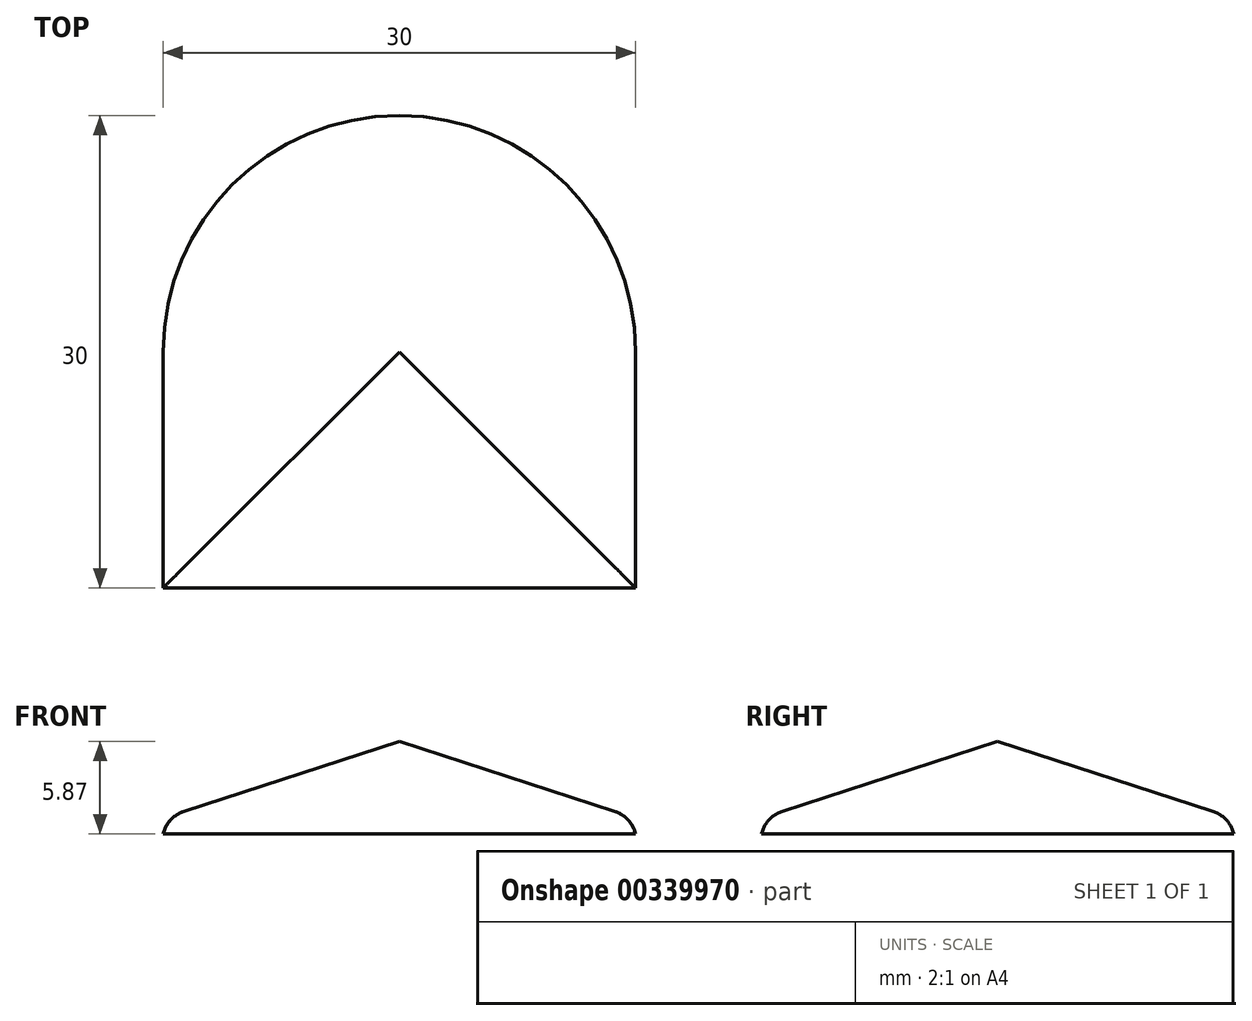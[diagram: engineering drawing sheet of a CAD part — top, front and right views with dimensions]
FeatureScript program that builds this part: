
annotation { "Feature Type Name" : "Feature", "Feature Type Description" : "" }
export const myFeature = defineFeature(function(context is Context, id is Id, definition is map)
    precondition{}
    {
        {
            var Q0;
            Q0=qCreatedBy(makeId("Top.planeOp"),FACE);
            var sketch = newSketch(context, id + "F0", { "sketchPlane" : qUnion([Q0])});
            skLineSegment(sketch, "E0.bottom", {"start": v(0, 15) * mm, "end": v(0, 15) * mm});
            skLineSegment(sketch, "E0.top", {"start": v(-15, -15) * mm, "end": v(15, -15) * mm});
            skLineSegment(sketch, "E0.left", {"start": v(-15, 0) * mm, "end": v(-15, -15) * mm});
            skLineSegment(sketch, "E0.right", {"start": v(15, 0) * mm, "end": v(15, -15) * mm});
            skPoint(sketch, "E0.middle", {"position": v(0, 0) * mm});
            skPoint(sketch, "E1.visualSharp", {"position": v(-15, 15) * mm});
            skArc(sketch, "E1.filletArc", {"start": v(0, 15) * mm, "mid": v(-10.6, 10.6) * mm, "end": v(-15, 0) * mm});
            skPoint(sketch, "E2.visualSharp", {"position": v(15, 15) * mm});
            skArc(sketch, "E2.filletArc", {"start": v(15, 0) * mm, "mid": v(10.6, 10.6) * mm, "end": v(0, 15) * mm});
            skSolve(sketch);
        }
        {
            var Q0;
            Q0 = qSketchRegion(id + "F0", true);
            extrude(context, id + "F1", {"entities" : qUnion([Q0]), "depth" : 5 * mm, "offsetDistance" : 25 * mm, "hasDraft" : true, "draftAngle" : 72 * degree, "draftPullDirection" : true});
        }
        {
            var Q0;
            Q0=makeQuery(id+"F1.opExtrude","CAP_FACE",FACE,{"disambiguationData":[OSD([sQuery(id+"F0.wireOp",EDGE,"E0.top"),sQuery(id+"F0.wireOp",EDGE,"E0.left"),sQuery(id+"F0.wireOp",EDGE,"E0.right"),sQuery(id+"F0.wireOp",EDGE,"E1.filletArc"),sQuery(id+"F0.wireOp",EDGE,"E2.filletArc")])],"isStart":true});
            extrude(context, id + "F2", {"entities" : qUnion([Q0]), "operationType" : NewBodyOperationType.ADD, "depth" : 1 * mm, "offsetDistance" : 25 * mm});
        }
        {
            var Q0;
            {var subQ0=sQuery(id+"F0.wireOp",EDGE,"E2.filletArc");var subQ1=sQuery(id+"F0.wireOp",EDGE,"E1.filletArc");Q0=makeQuery(id+"F2.boolean.opBoolean","MERGE",EDGE,{"derivedFrom":[makeQuery(id+"F1.opExtrude","CAP_EDGE",EDGE,{"disambiguationData":[OSD([subQ1,subQ0])],"isStart":true}),makeQuery(id+"F2.opExtrude","CAP_EDGE",EDGE,{"disambiguationData":[OSD([subQ1,subQ0])],"isStart":true})]});}
            var Q1;
            {var subQ0=sQuery(id+"F0.wireOp",EDGE,"E0.top");Q1=makeQuery(id+"F2.boolean.opBoolean","MERGE",EDGE,{"derivedFrom":[makeQuery(id+"F1.opExtrude","CAP_EDGE",EDGE,{"disambiguationData":[OSD([subQ0])],"isStart":true}),makeQuery(id+"F2.opExtrude","CAP_EDGE",EDGE,{"disambiguationData":[OSD([subQ0])],"isStart":true})]});}
            fillet(context, id + "F3", {"entities" : qUnion([Q0, Q1]), "radius" : 2 * mm, "tangentPropagation" : true, "allowEdgeOverflow" : false});
        }
    });
